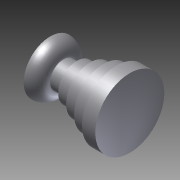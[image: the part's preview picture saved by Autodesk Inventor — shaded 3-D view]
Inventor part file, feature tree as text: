
AUTODESK INVENTOR PART (.ipt)
format: ipt  version: 2011 SP1 (Build 150282100, 282)  size: 125,440 bytes
history: native  units: mm
features: revolve x1, sketch x1
ambient origin geometry x8: Origin, YZ Plane, XZ Plane, XY Plane, X Axis, Y Axis, Z Axis, Center Point
bodies: Solid1 (feature_tree)
feature tree (2):
  revolve  "Revolution1"  [1 undecoded]
  sketch  "Sketch1"  dims[d2=5.0mm d3=5.0mm d4=5.0mm d5=5.0mm d7=5.0mm d8=2.0mm d9=2.0mm d10=2.0mm d11=2.0mm d12=10.0mm d13=90.0deg]
note: 1 required parameter value undecoded (feature->parameter linkage not recoverable at this tier; creation-order binding heuristic only, values carry confidence <= 0.55)
